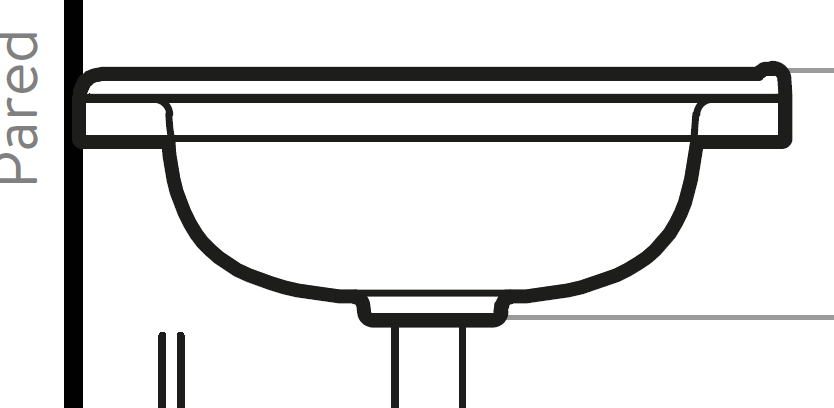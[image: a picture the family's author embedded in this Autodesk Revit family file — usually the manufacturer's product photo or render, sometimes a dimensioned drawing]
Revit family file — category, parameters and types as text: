
# Revit family: 603276091_Mueble Aluvia Habano a Piso 40x35
name_source: partatom
category: Plumbing Fixtures
units: mm (PartAtom-declared; Revit-internal decimal feet)

## family parameters
Always vertical = Yes
Cut with Voids When Loaded = No
OmniClass Number = 23.31.13.11
OmniClass Title = Single Sinks
Part Type = Normal
Room Calculation Point = No
Round Connector Dimension = Use Diameter
Shared = No
Work Plane-Based = Yes

## types (2) — shared parameters
Alto = 850 mm  [stored 2.78871 ft]
Ancho = 395 mm  [stored 1.29593 ft]
Canto = PVC rígido 2 mm de calibre.
Carga máxima = 77,2 lb (35 kg).
Default Elevation = 1219 mm
Densidad = 15 mms 670 kg./m^3.
Description = La línea ALUVIA viene a entregar de manera asequible una solución perfecta que combina
diseño y funcionalidad, ALUVIA se inspira en el movimiento y caída del agua en la
naturaleza, es por ello de sus formas orgánicas donde podemos obtener un producto
compacto y de líneas fluidas, que se adapta en espacios pequeños.
el pricipal benefico de los muebles de esta linea es ser un producto compacto que cuenta
con cajón y repisa brindándole al consumidor mayor capacidad de almacenamiento,
brindando una excelente solución para aquellos espacios pequeños.
· Mueble compacto para espacios pequeños.
· Lavamanos 100% en porcelana.
· Grán capacidad de almacenamiento.
Dimensiones Generales (H * W * P) = 33,46” x 15,55” x 13,58” (850 x 395 x 345 mm).
Garantia Herrajes = 1 año
Garantia Madera = 1 año
Manufacturer = Corona
Material Lavamanos = Corona_Cerámica_Sinterizada
Material madera interior = Corona_Madera_Aglomerada_Plomo
Model = Mueble aluvia miel LVM 45X45
Patas = Corona_Acero
Peso Bruto aprox = 35,9 lb (16,3 kg).
Peso Neto aprox = 33,5 lb (15,2 kg).
Pieza en U = Corona_Poliestrieno_Gris
Profundidad = 350 mm  [stored 1.14829 ft]
Resistencia a la humedad = 8%
Resistencia al rayado = 700 ciclos
Textura = Habano: Poro - Gris: Soft
Miel:poro - Plomo:mate.
URL = https://corona.co

## per-type parameters (varying)
| type | Material |
| Ref. 603271711 Mueble Aluvia Miel Con Lavamanos | Corona_Madera_Aglomerada_Miel |
| Ref. 603276091 Mueble Aluvia Habano Con Lavamanos | Corona_Madera_Aglomerada_Habano |

note: [stored X ft] marks values corroborated as IEEE doubles in the binary element streams (Revit-internal decimal feet)

## geometry (parser evidence)
native form markers: Blend x4, Extrusion x1, Sweep x34
no freeform markers — native parametric forms only
